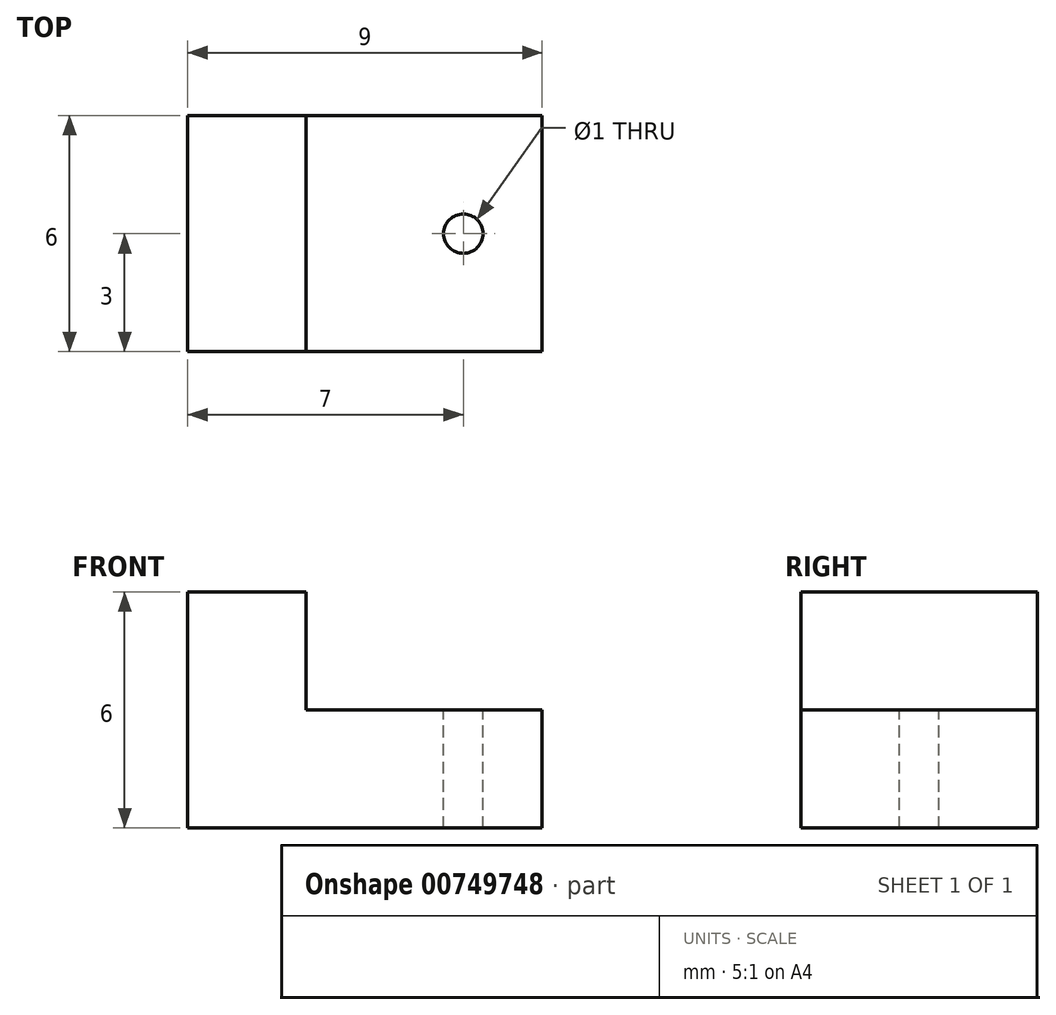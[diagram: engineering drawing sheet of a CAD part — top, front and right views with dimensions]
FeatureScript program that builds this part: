
annotation { "Feature Type Name" : "Feature", "Feature Type Description" : "" }
export const myFeature = defineFeature(function(context is Context, id is Id, definition is map)
    precondition{}
    {
        {
            var Q0;
            Q0=qCreatedBy(makeId("Front.planeOp"),FACE);
            var sketch = newSketch(context, id + "F0", { "sketchPlane" : qUnion([Q0])});
            skLineSegment(sketch, "E0", {"start": v(0, 0) * mm, "end": v(0, -6) * mm});
            skLineSegment(sketch, "E1", {"start": v(0, -6) * mm, "end": v(9, -6) * mm});
            skLineSegment(sketch, "E2", {"start": v(9, -6) * mm, "end": v(9, -3) * mm});
            skLineSegment(sketch, "E3", {"start": v(9, -3) * mm, "end": v(3, -3) * mm});
            skLineSegment(sketch, "E4", {"start": v(3, -3) * mm, "end": v(3, 0) * mm});
            skLineSegment(sketch, "E5", {"start": v(3, 0) * mm, "end": v(0, 0) * mm});
            skSolve(sketch);
        }
        {
            var Q0;
            Q0 = qSketchRegion(id + "F0", true);
            extrude(context, id + "F1", {"entities" : qUnion([Q0]), "depth" : 6 * mm, "offsetDistance" : 25 * mm});
        }
        {
            var Q0;
            Q0=makeQuery(id+"F1.opExtrude","SWEPT_FACE",FACE,{"disambiguationData":[OSD([sQuery(id+"F0.wireOp",EDGE,"E3")])]});
            var sketch = newSketch(context, id + "F2", { "sketchPlane" : qUnion([Q0])});
            skCircle(sketch, "E6", {"center": v(7, -3) * mm, "radius": 0.5 * mm});
            skPoint(sketch, "E6.centerSnap0", {"position": v(7, 0) * mm});
            skPoint(sketch, "E6.centerSnap1", {"position": v(9, -3) * mm});
            skSolve(sketch);
        }
        {
            var Q0;
            Q0 = qSketchRegion(id + "F2", true);
            extrude(context, id + "F3", {"entities" : qUnion([Q0]), "operationType" : NewBodyOperationType.REMOVE, "endBound" : BoundingType.THROUGH_ALL, "oppositeDirection" : true, "depth" : 25 * mm, "offsetDistance" : 25 * mm});
        }
    });
